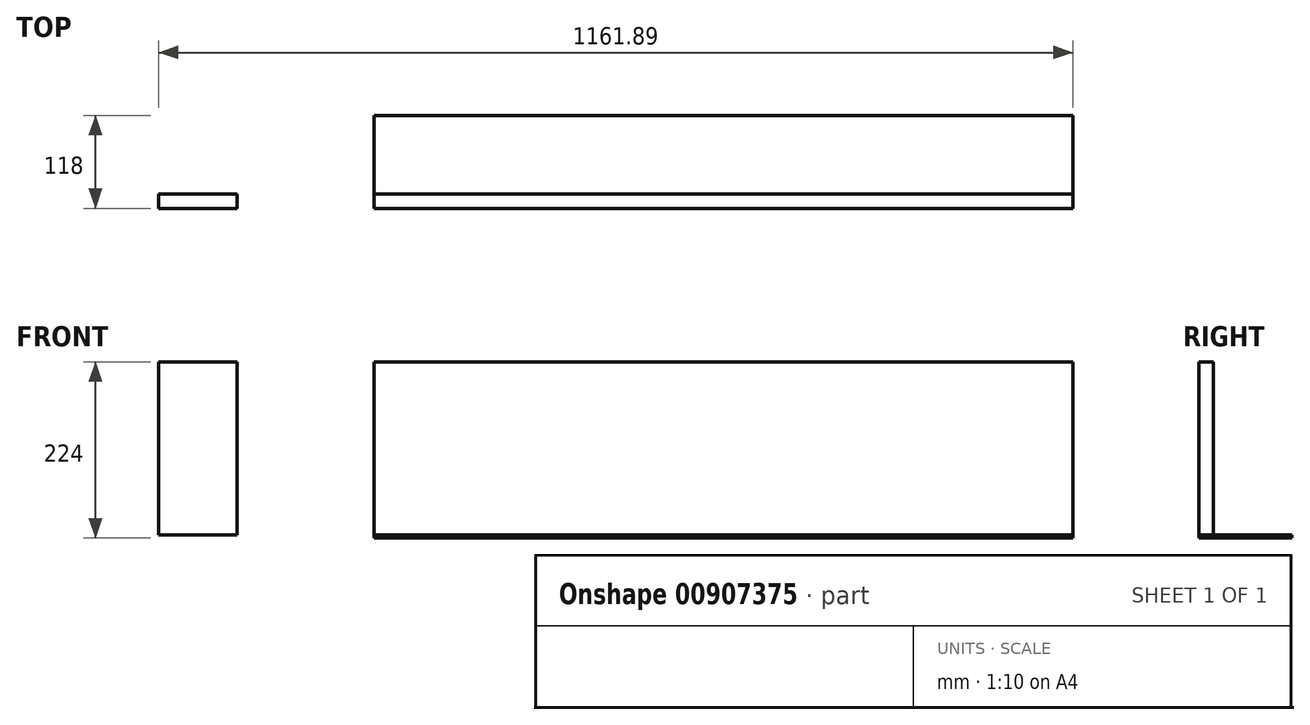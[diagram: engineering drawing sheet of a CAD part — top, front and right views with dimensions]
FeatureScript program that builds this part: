
annotation { "Feature Type Name" : "Feature", "Feature Type Description" : "" }
export const myFeature = defineFeature(function(context is Context, id is Id, definition is map)
    precondition{}
    {
        {
            var Q0;
            Q0=qCreatedBy(makeId("Front.planeOp"),FACE);
            var sketch = newSketch(context, id + "F0", { "sketchPlane" : qUnion([Q0])});
            skLineSegment(sketch, "E0.bottom", {"start": v(-433.18, -139.22) * mm, "end": v(454.82, -139.22) * mm});
            skLineSegment(sketch, "E0.top", {"start": v(-433.18, 80.78) * mm, "end": v(454.82, 80.78) * mm});
            skLineSegment(sketch, "E0.left", {"start": v(-433.18, -139.22) * mm, "end": v(-433.18, 80.78) * mm});
            skLineSegment(sketch, "E0.right", {"start": v(454.82, -139.22) * mm, "end": v(454.82, 80.78) * mm});
            skLineSegment(sketch, "E1.bottom", {"start": v(-607.07, -139.22) * mm, "end": v(-707.07, -139.22) * mm});
            skLineSegment(sketch, "E1.top", {"start": v(-607.07, 80.78) * mm, "end": v(-707.07, 80.78) * mm});
            skLineSegment(sketch, "E1.left", {"start": v(-607.07, -139.22) * mm, "end": v(-607.07, 80.78) * mm});
            skLineSegment(sketch, "E1.right", {"start": v(-707.07, -139.22) * mm, "end": v(-707.07, 80.78) * mm});
            skSolve(sketch);
        }
        {
            var Q0;
            Q0 = qSketchRegion(id + "F0", true);
            extrude(context, id + "F1", {"entities" : qUnion([Q0]), "depth" : 18 * mm, "offsetDistance" : 25 * mm});
        }
        {
            var Q0;
            Q0=makeQuery(id+"F1.opExtrude","SWEPT_FACE",FACE,{"disambiguationData":[OSD([sQuery(id+"F0.wireOp",EDGE,"E0.bottom")])]});
            var sketch = newSketch(context, id + "F2", { "sketchPlane" : qUnion([Q0])});
            skLineSegment(sketch, "E2.bottom", {"start": v(-433.18, 18) * mm, "end": v(454.82, 18) * mm});
            skLineSegment(sketch, "E2.top", {"start": v(-433.18, -100) * mm, "end": v(454.82, -100) * mm});
            skLineSegment(sketch, "E2.left", {"start": v(-433.18, 18) * mm, "end": v(-433.18, -100) * mm});
            skLineSegment(sketch, "E2.right", {"start": v(454.82, 18) * mm, "end": v(454.82, -100) * mm});
            skSolve(sketch);
        }
        {
            var Q0;
            Q0 = qSketchRegion(id + "F2", true);
            extrude(context, id + "F3", {"entities" : qUnion([Q0]), "depth" : 4 * mm, "offsetDistance" : 25 * mm});
        }
    });
